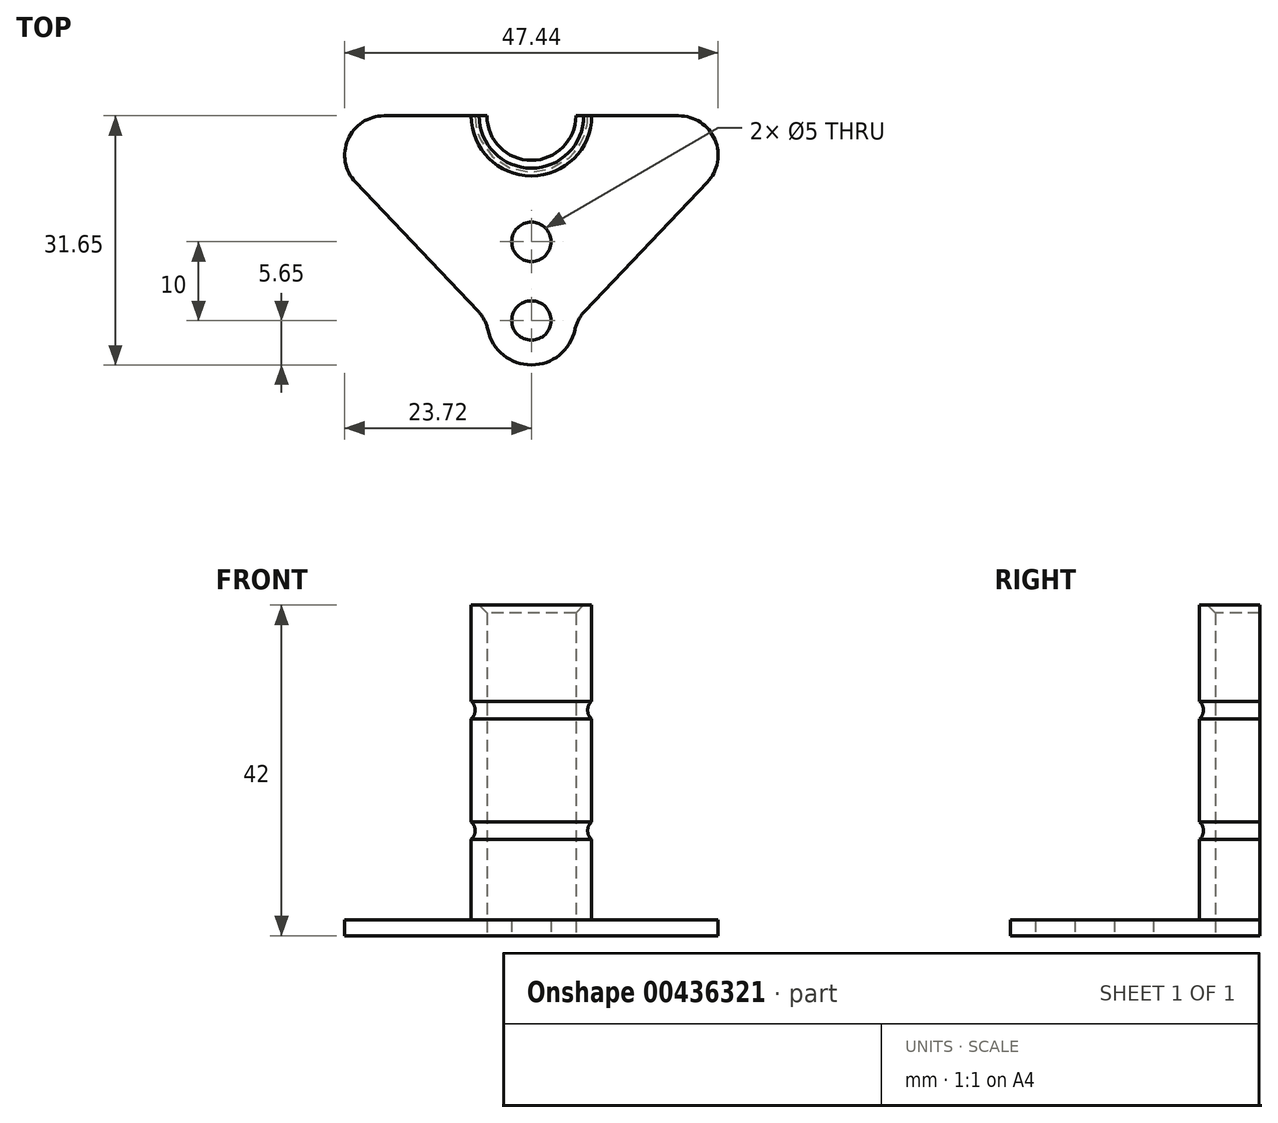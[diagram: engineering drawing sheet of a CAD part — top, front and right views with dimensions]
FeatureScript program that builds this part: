
annotation { "Feature Type Name" : "Feature", "Feature Type Description" : "" }
export const myFeature = defineFeature(function(context is Context, id is Id, definition is map)
    precondition{}
    {
        {
            assignVariable(context, id + "F0", {"name" : "WallThick", "anyValue" : 2});
        }
        {
            assignVariable(context, id + "F1", {"name" : "CableChannelHeight", "anyValue" : 40});
        }
        {
            var Q0;
            Q0=qCreatedBy(makeId("Top.planeOp"),FACE);
            var sketch = newSketch(context, id + "F2", { "sketchPlane" : qUnion([Q0])});
            skCircle(sketch, "E0", {"center": v(0, 0) * mm, "radius": 5.65 * mm, "construction": true});
            skArc(sketch, "E1", {"start": v(-5.65, 0) * mm, "mid": v(0, -5.65) * mm, "end": v(5.65, 0) * mm});
            skLineSegment(sketch, "E2", {"start": v(-5.65, 0) * mm, "end": v(-30.37, 0) * mm});
            skLineSegment(sketch, "E3", {"start": v(-30.37, 0) * mm, "end": v(-5.65, -26) * mm});
            skArc(sketch, "E4", {"start": v(-5.65, -26) * mm, "mid": v(0, -31.65) * mm, "end": v(5.65, -26) * mm});
            skLineSegment(sketch, "E5", {"start": v(5.65, -26) * mm, "end": v(30.37, 0) * mm});
            skLineSegment(sketch, "E6", {"start": v(30.37, 0) * mm, "end": v(5.65, 0) * mm});
            skCircle(sketch, "E7", {"center": v(0, -26) * mm, "radius": 2.5 * mm});
            skLineSegment(sketch, "E8", {"start": v(0, -26) * mm, "end": v(0, -16) * mm, "construction": true});
            skLineSegment(sketch, "E9", {"start": v(0, -16) * mm, "end": v(0, 0) * mm, "construction": true});
            skCircle(sketch, "E10", {"center": v(0, -16) * mm, "radius": 2.5 * mm});
            skSolve(sketch);
        }
        {
            var Q0;
            Q0=makeQuery(id+"F2.imprint","IMPRINT",FACE,{"disambiguationData":[TD([[makeQuery(id+"F2.imprint","IMPRINT",EDGE,{"derivedFrom":sQuery(id+"F2.wireOp",EDGE,"E1")}),-1.0]])]});
            extrude(context, id + "F3", {"entities" : qUnion([Q0]), "depth" : (getVariable(context, 'WallThick')) * mm});
        }
        {
            var Q0;
            Q0=makeQuery(id+"F3.opExtrude","CAP_FACE",FACE,{"disambiguationData":[OSD([sQuery(id+"F2.wireOp",EDGE,"E1"),sQuery(id+"F2.wireOp",EDGE,"E2"),sQuery(id+"F2.wireOp",EDGE,"E3"),sQuery(id+"F2.wireOp",EDGE,"E4"),sQuery(id+"F2.wireOp",EDGE,"E5"),sQuery(id+"F2.wireOp",EDGE,"E6"),sQuery(id+"F2.wireOp",EDGE,"E7"),sQuery(id+"F2.wireOp",EDGE,"E10")])],"isStart":false});
            var sketch = newSketch(context, id + "F4", { "sketchPlane" : qUnion([Q0])});
            skArc(sketch, "E11.0", {"start": v(-5.65, 0) * mm, "mid": v(0, -5.65) * mm, "end": v(5.65, 0) * mm});
            skArc(sketch, "E12.0", {"start": v(-7.65, 0) * mm, "mid": v(0, -7.65) * mm, "end": v(7.65, 0) * mm});
            skLineSegment(sketch, "E13", {"start": v(-7.65, 0) * mm, "end": v(-5.65, 0) * mm});
            skLineSegment(sketch, "E14", {"start": v(5.65, 0) * mm, "end": v(7.65, 0) * mm});
            skSolve(sketch);
        }
        {
            var Q0;
            Q0 = qSketchRegion(id + "F4", true);
            extrude(context, id + "F5", {"entities" : qUnion([Q0]), "operationType" : NewBodyOperationType.ADD, "depth" : (getVariable(context, 'CableChannelHeight')) * mm});
        }
        {
            var Q0;
            Q0=makeQuery(id+"F5.opExtrude","CAP_EDGE",EDGE,{"disambiguationData":[OSD([sQuery(id+"F4.wireOp",EDGE,"E12.0")])],"isStart":true});
            var Q1;
            Q1=makeQuery(id+"F3.opExtrude","SWEPT_EDGE",EDGE,{"disambiguationData":[OSD([sQuery(id+"F2.wireOp",EDGE,"E2"),sQuery(id+"F2.wireOp",EDGE,"E3")])]});
            var Q2;
            Q2=makeQuery(id+"F3.opExtrude","SWEPT_EDGE",EDGE,{"disambiguationData":[OSD([sQuery(id+"F2.wireOp",EDGE,"E3"),sQuery(id+"F2.wireOp",EDGE,"E4")])]});
            var Q3;
            Q3=makeQuery(id+"F3.opExtrude","SWEPT_EDGE",EDGE,{"disambiguationData":[OSD([sQuery(id+"F2.wireOp",EDGE,"E4"),sQuery(id+"F2.wireOp",EDGE,"E5")])]});
            var Q4;
            Q4=makeQuery(id+"F3.opExtrude","SWEPT_EDGE",EDGE,{"disambiguationData":[OSD([sQuery(id+"F2.wireOp",EDGE,"E5"),sQuery(id+"F2.wireOp",EDGE,"E6")])]});
            fillet(context, id + "F6", {"entities" : qUnion([Q0, Q1, Q2, Q3, Q4]), "radius" : 5 * mm, "tangentPropagation" : true, "allowEdgeOverflow" : false});
        }
        {
            var Q0;
            Q0=makeQuery(id+"F5.boolean.opBoolean","MERGE",FACE,{"derivedFrom":[makeQuery(id+"F3.opExtrude","SWEPT_FACE",FACE,{"disambiguationData":[OSD([sQuery(id+"F2.wireOp",EDGE,"E2")])]}),makeQuery(id+"F5.opExtrude","SWEPT_FACE",FACE,{"disambiguationData":[OSD([sQuery(id+"F4.wireOp",EDGE,"E13")])]})]});
            var sketch = newSketch(context, id + "F7", { "sketchPlane" : qUnion([Q0])});
            skLineSegment(sketch, "E15", {"start": v(5.65, 0) * mm, "end": v(5.65, 13.33) * mm, "construction": true});
            skLineSegment(sketch, "E16", {"start": v(5.65, 13.33) * mm, "end": v(8.65, 13.33) * mm, "construction": true});
            skLineSegment(sketch, "E17", {"start": v(8.65, 11.83) * mm, "end": v(8.65, 14.83) * mm});
            skArc(sketch, "E18", {"start": v(8.65, 14.83) * mm, "mid": v(7.15, 13.33) * mm, "end": v(8.65, 11.83) * mm});
            skLineSegment(sketch, "E19.0", {"start": v(-5.65, 42) * mm, "end": v(-5.65, 0) * mm, "construction": true});
            skLineSegment(sketch, "E20", {"start": v(-5.65, 21) * mm, "end": v(5.65, 21) * mm, "construction": true});
            skArc(sketch, "E21.MirrorCS", {"start": v(8.65, 27.17) * mm, "mid": v(7.15, 28.67) * mm, "end": v(8.65, 30.17) * mm});
            skLineSegment(sketch, "E22.MirrorCS", {"start": v(8.65, 30.17) * mm, "end": v(8.65, 27.17) * mm});
            skLineSegment(sketch, "E23", {"start": v(0, 21) * mm, "end": v(0, 0) * mm, "construction": true});
            skLineSegment(sketch, "E24", {"start": v(6.65, 42) * mm, "end": v(5.65, 41) * mm});
            skLineSegment(sketch, "E25", {"start": v(5.65, 41) * mm, "end": v(5.65, 42) * mm});
            skLineSegment(sketch, "E26", {"start": v(5.65, 42) * mm, "end": v(6.65, 42) * mm});
            skSolve(sketch);
        }
        {
            var Q0;
            Q0 = qSketchRegion(id + "F7", true);
            var Q1;
            Q1=sQuery(id+"F7.wireOp",EDGE,"E23");
            revolve(context, id + "F8", {"operationType" : NewBodyOperationType.REMOVE, "entities" : qUnion([Q0]), "axis" : qUnion([Q1]), "revolveType" : RevolveType.FULL, "oppositeDirection" : true});
        }
    });
